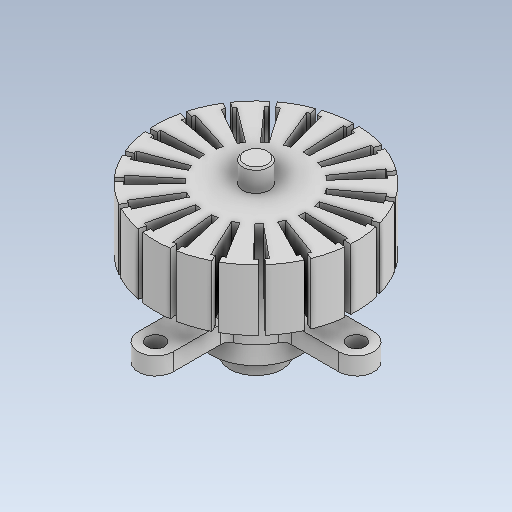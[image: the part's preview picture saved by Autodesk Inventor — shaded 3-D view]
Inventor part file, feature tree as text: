
AUTODESK INVENTOR PART (.ipt)
format: ipt  version: 2020 (Build 240168000, 168)  size: 391,168 bytes
history: native  units: mm
features: sketch x8, extrude x7, projected_geometry x3, hole x1, fillet x1, pattern_circular x1, plane x1, chamfer x1
ambient origin geometry x8: Origin, YZ Plane, XZ Plane, XY Plane, X Axis, Y Axis, Z Axis, Center Point
bodies: Solid1 (feature_tree)
feature tree (23):
  extrude  "Extrusion1"  Depth=5.0mm TaperAngle=0.0deg
  extrude  "Extrusion2"  Depth=2.5mm TaperAngle=0.0deg
  extrude  "Extrusion3"  Depth=1.7mm TaperAngle=0.0deg
  extrude  "Extrusion4"  Depth=11.5mm
  hole  "Hole1"  [1 undecoded]
  fillet  "Fillet1"  Radius=23.0mm
  extrude  "Extrusion5"  Depth=2.0mm TaperAngle=0.0deg
  extrude  "Extrusion6"  Depth=1.0mm
  pattern_circular  "Circular Pattern1"  [2 undecoded]
  sketch  "Sketch8"  dims[d25=6.0mm d26=4.2mm d27=0.0mm d28=23.0mm d29=1.047198mm d30=1.047198mm d31=0.8mm d32=0.349066mm d33=0.349066mm d34=7.0mm d35=0.0mm d36=190.0mm d37=360.0deg d39=3.0mm d40=7.0mm d41=0.0mm d42=0.2mm d43=2.0mm d44=45.0deg]
  plane  "Work Plane1"
  extrude  "Extrusion7"  Depth=2.0mm
  chamfer  "Chamfer1"  Distance=1.047198mm
  sketch  "Sketch1"  dims[d0=11.5mm d1=5.0mm d2=0.0mm]
  sketch  "Sketch2"  dims[d3=10.3mm d4=2.5mm d5=0.0mm]
  sketch  "Sketch3"  dims[d6=1.35mm d7=1.7mm d8=0.0mm]
  projected_geometry  "Projected Loop1"
  sketch  "Sketch4"  dims[d9=11.5mm d10=23.0mm]
  sketch  "Sketch5"  dims[d11=4.0mm d12=11.5mm d13=23.0mm]
  projected_geometry  "Projected Loop2"
  sketch  "Sketch6"  dims[d14=4.0mm d15=2.0mm d16=0.0mm]
  sketch  "Sketch7"  dims[d17=2.0mm d18=6.0mm d19=4.0mm d20=2.0mm d21=90.0deg d22=5.0mm d23=0.0mm d24=1.0mm]
  projected_geometry  "Projected Loop3"
note: 3 required parameter values undecoded (feature->parameter linkage not recoverable at this tier; creation-order binding heuristic only, values carry confidence <= 0.55)
